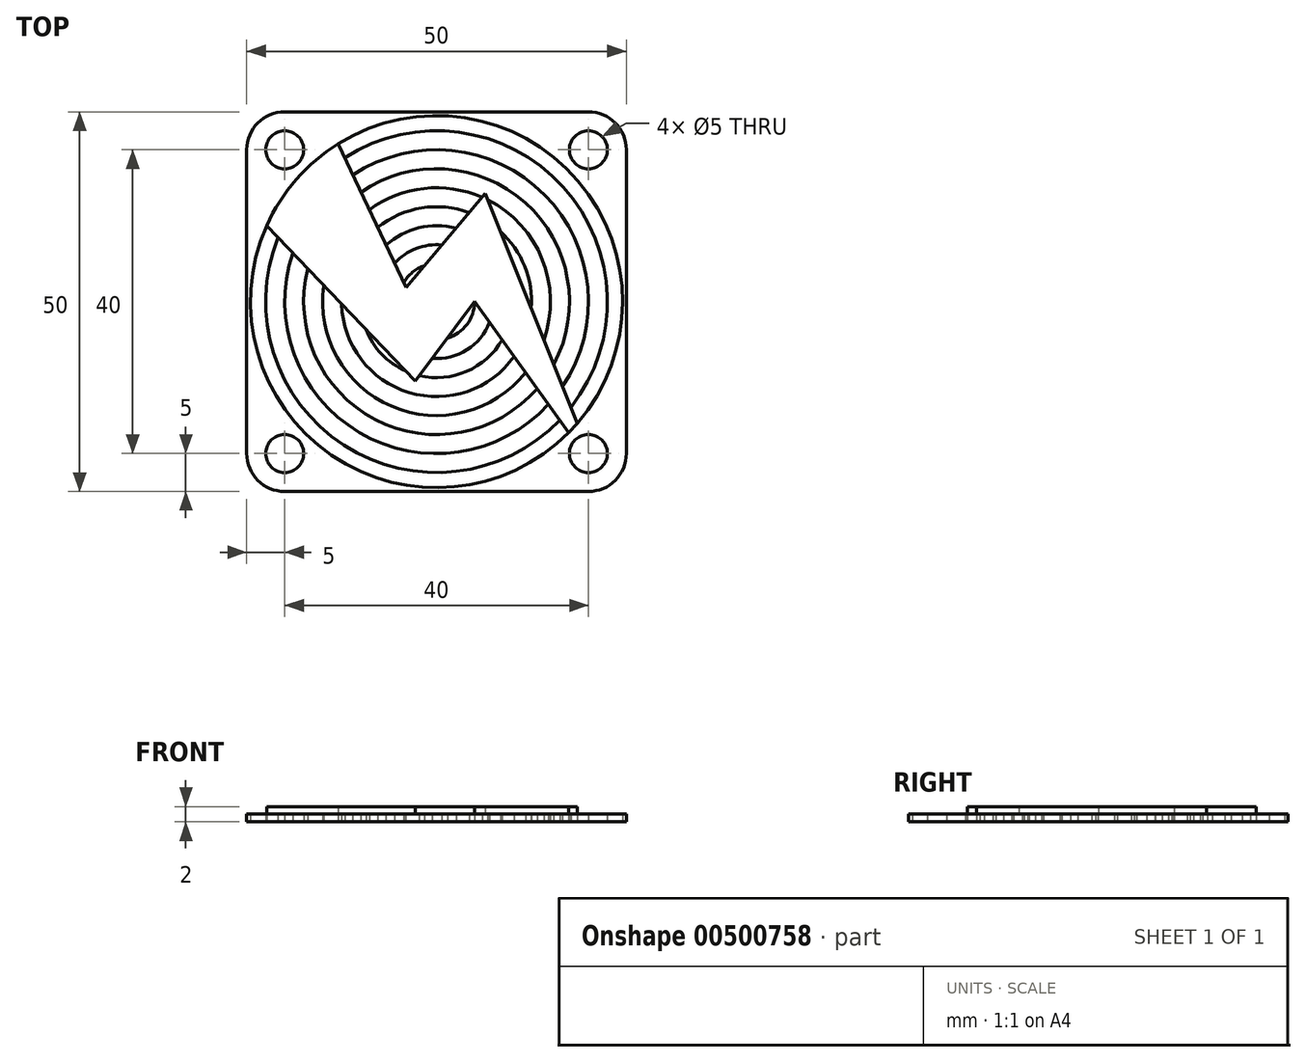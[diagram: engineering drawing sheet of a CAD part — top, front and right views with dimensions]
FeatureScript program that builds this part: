
annotation { "Feature Type Name" : "Feature", "Feature Type Description" : "" }
export const myFeature = defineFeature(function(context is Context, id is Id, definition is map)
    precondition{}
    {
        {
            var Q0;
            Q0=qCreatedBy(makeId("Top.planeOp"),FACE);
            var sketch = newSketch(context, id + "F0", { "sketchPlane" : qUnion([Q0])});
            skLineSegment(sketch, "E0.bottom", {"start": v(-25, 25) * mm, "end": v(25, 25) * mm});
            skLineSegment(sketch, "E0.top", {"start": v(-25, -25) * mm, "end": v(25, -25) * mm});
            skLineSegment(sketch, "E0.left", {"start": v(-25, 25) * mm, "end": v(-25, -25) * mm});
            skLineSegment(sketch, "E0.right", {"start": v(25, 25) * mm, "end": v(25, -25) * mm});
            skCircle(sketch, "E1", {"center": v(20, 20) * mm, "radius": 2.5 * mm});
            skCircle(sketch, "E2", {"center": v(20, -20) * mm, "radius": 2.5 * mm});
            skCircle(sketch, "E3", {"center": v(-20, -20) * mm, "radius": 2.5 * mm});
            skCircle(sketch, "E4", {"center": v(-20, 20) * mm, "radius": 2.5 * mm});
            skCircle(sketch, "E5", {"center": v(0, 0) * mm, "radius": 24.5 * mm});
            skLineSegment(sketch, "E6", {"start": v(-12.96, 20.8) * mm, "end": v(-4.03, 1.85) * mm});
            skLineSegment(sketch, "E7", {"start": v(-4.03, 1.85) * mm, "end": v(6.41, 14.23) * mm});
            skLineSegment(sketch, "E8", {"start": v(6.41, 14.23) * mm, "end": v(21.03, -22.28) * mm});
            skLineSegment(sketch, "E9", {"start": v(21.03, -22.28) * mm, "end": v(5.04, 0) * mm});
            skLineSegment(sketch, "E10", {"start": v(5.04, 0) * mm, "end": v(-2.81, -10.46) * mm});
            skLineSegment(sketch, "E11", {"start": v(-2.81, -10.46) * mm, "end": v(-22.38, 9.98) * mm});
            skCircle(sketch, "E12", {"center": v(0, 0) * mm, "radius": 7.5 * mm});
            skCircle(sketch, "E13", {"center": v(0, 0) * mm, "radius": 10 * mm});
            skCircle(sketch, "E14", {"center": v(0, 0) * mm, "radius": 12.5 * mm});
            skCircle(sketch, "E15", {"center": v(0, 0) * mm, "radius": 15 * mm});
            skCircle(sketch, "E16", {"center": v(0, 0) * mm, "radius": 17.5 * mm});
            skCircle(sketch, "E17", {"center": v(0, 0) * mm, "radius": 20 * mm});
            skCircle(sketch, "E18", {"center": v(0, 0) * mm, "radius": 22.5 * mm});
            skCircle(sketch, "E19", {"center": v(0, 0) * mm, "radius": 5 * mm});
            skCircle(sketch, "E20", {"center": v(-20, 20) * mm, "radius": 3.5 * mm});
            skCircle(sketch, "E21", {"center": v(20, 20) * mm, "radius": 3.5 * mm});
            skCircle(sketch, "E22", {"center": v(20, -20) * mm, "radius": 3.5 * mm});
            skCircle(sketch, "E23", {"center": v(-20, -20) * mm, "radius": 3.5 * mm});
            skSolve(sketch);
        }
        {
            var Q0;
            Q0=makeQuery(id+"F0.imprint","IMPRINT",FACE,{"disambiguationData":[TD([[makeQuery(id+"F0.imprint","IMPRINT",EDGE,{"derivedFrom":sQuery(id+"F0.wireOp",EDGE,"E0.bottom")}),-1.0]])]});
            var Q1;
            {var subQ0=sQuery(id+"F0.wireOp",EDGE,"E6");var subQ1=sQuery(id+"F0.wireOp",EDGE,"E5");var subQ2=makeQuery(id+"F0.imprint","INTERSECT",VERTEX,{"derivedFrom":[subQ1,subQ0]});Q1=makeQuery(id+"F0.imprint","IMPRINT",FACE,{"disambiguationData":[TD([[makeQuery(id+"F0.imprint","IMPRINT",EDGE,{"disambiguationData":[TD([[subQ2,-1.0]])],"derivedFrom":subQ1}),1.0]])]});}
            var Q2;
            {var subQ0=sQuery(id+"F0.wireOp",EDGE,"E18");var subQ1=sQuery(id+"F0.wireOp",EDGE,"E6");var subQ2=makeQuery(id+"F0.imprint","INTERSECT",VERTEX,{"derivedFrom":[subQ1,subQ0]});Q2=makeQuery(id+"F0.imprint","IMPRINT",FACE,{"disambiguationData":[TD([[makeQuery(id+"F0.imprint","IMPRINT",EDGE,{"disambiguationData":[TD([[subQ2,-1.0]])],"derivedFrom":subQ1}),-1.0]])]});}
            var Q3;
            {var subQ0=sQuery(id+"F0.wireOp",EDGE,"E17");var subQ1=sQuery(id+"F0.wireOp",EDGE,"E6");var subQ2=makeQuery(id+"F0.imprint","INTERSECT",VERTEX,{"derivedFrom":[subQ1,subQ0]});Q3=makeQuery(id+"F0.imprint","IMPRINT",FACE,{"disambiguationData":[TD([[makeQuery(id+"F0.imprint","IMPRINT",EDGE,{"disambiguationData":[TD([[subQ2,-1.0]])],"derivedFrom":subQ1}),-1.0]])]});}
            var Q4;
            {var subQ0=sQuery(id+"F0.wireOp",EDGE,"E16");var subQ1=sQuery(id+"F0.wireOp",EDGE,"E6");var subQ2=makeQuery(id+"F0.imprint","INTERSECT",VERTEX,{"derivedFrom":[subQ1,subQ0]});Q4=makeQuery(id+"F0.imprint","IMPRINT",FACE,{"disambiguationData":[TD([[makeQuery(id+"F0.imprint","IMPRINT",EDGE,{"disambiguationData":[TD([[subQ2,-1.0]])],"derivedFrom":subQ1}),-1.0]])]});}
            var Q5;
            {var subQ0=sQuery(id+"F0.wireOp",EDGE,"E15");var subQ1=sQuery(id+"F0.wireOp",EDGE,"E6");var subQ2=makeQuery(id+"F0.imprint","INTERSECT",VERTEX,{"derivedFrom":[subQ1,subQ0]});Q5=makeQuery(id+"F0.imprint","IMPRINT",FACE,{"disambiguationData":[TD([[makeQuery(id+"F0.imprint","IMPRINT",EDGE,{"disambiguationData":[TD([[subQ2,-1.0]])],"derivedFrom":subQ1}),-1.0]])]});}
            var Q6;
            {var subQ0=sQuery(id+"F0.wireOp",EDGE,"E14");var subQ1=sQuery(id+"F0.wireOp",EDGE,"E6");var subQ2=makeQuery(id+"F0.imprint","INTERSECT",VERTEX,{"derivedFrom":[subQ1,subQ0]});Q6=makeQuery(id+"F0.imprint","IMPRINT",FACE,{"disambiguationData":[TD([[makeQuery(id+"F0.imprint","IMPRINT",EDGE,{"disambiguationData":[TD([[subQ2,-1.0]])],"derivedFrom":subQ1}),-1.0]])]});}
            var Q7;
            {var subQ0=sQuery(id+"F0.wireOp",EDGE,"E13");var subQ8=sQuery(id+"F0.wireOp",EDGE,"E6");var subQ10=makeQuery(id+"F0.imprint","INTERSECT",VERTEX,{"derivedFrom":[subQ8,subQ0]});Q7=makeQuery(id+"F0.imprint","IMPRINT",FACE,{"disambiguationData":[TD([[makeQuery(id+"F0.imprint","IMPRINT",EDGE,{"disambiguationData":[TD([[subQ10,-1.0]])],"derivedFrom":subQ8}),-1.0]])]});}
            var Q8;
            {var subQ0=sQuery(id+"F0.wireOp",EDGE,"E12");var subQ1=sQuery(id+"F0.wireOp",EDGE,"E6");var subQ2=makeQuery(id+"F0.imprint","INTERSECT",VERTEX,{"derivedFrom":[subQ1,subQ0]});Q8=makeQuery(id+"F0.imprint","IMPRINT",FACE,{"disambiguationData":[TD([[makeQuery(id+"F0.imprint","IMPRINT",EDGE,{"disambiguationData":[TD([[subQ2,-1.0]])],"derivedFrom":subQ1}),-1.0]])]});}
            var Q9;
            {var subQ1=sQuery(id+"F0.wireOp",EDGE,"E6");var subQ5=sQuery(id+"F0.wireOp",EDGE,"E7");var subQ6=makeQuery(id+"F0.imprint","INTERSECT",VERTEX,{"derivedFrom":[subQ1,subQ5]});Q9=makeQuery(id+"F0.imprint","IMPRINT",FACE,{"disambiguationData":[TD([[makeQuery(id+"F0.imprint","IMPRINT",EDGE,{"disambiguationData":[TD([[subQ6,1.0]])],"derivedFrom":subQ1}),-1.0]])]});}
            var Q10;
            {var subQ1=sQuery(id+"F0.wireOp",EDGE,"E7");var subQ7=sQuery(id+"F0.wireOp",EDGE,"E19");var subQ9=makeQuery(id+"F0.imprint","INTERSECT",VERTEX,{"derivedFrom":[subQ1,subQ7]});Q10=makeQuery(id+"F0.imprint","IMPRINT",FACE,{"disambiguationData":[TD([[makeQuery(id+"F0.imprint","IMPRINT",EDGE,{"disambiguationData":[TD([[subQ9,-1.0]])],"derivedFrom":subQ1}),-1.0]])]});}
            var Q11;
            {var subQ0=sQuery(id+"F0.wireOp",EDGE,"E12");var subQ1=sQuery(id+"F0.wireOp",EDGE,"E7");var subQ2=makeQuery(id+"F0.imprint","INTERSECT",VERTEX,{"derivedFrom":[subQ1,subQ0]});Q11=makeQuery(id+"F0.imprint","IMPRINT",FACE,{"disambiguationData":[TD([[makeQuery(id+"F0.imprint","IMPRINT",EDGE,{"disambiguationData":[TD([[subQ2,-1.0]])],"derivedFrom":subQ1}),-1.0]])]});}
            var Q12;
            {var subQ0=sQuery(id+"F0.wireOp",EDGE,"E13");var subQ1=sQuery(id+"F0.wireOp",EDGE,"E7");var subQ2=makeQuery(id+"F0.imprint","INTERSECT",VERTEX,{"derivedFrom":[subQ1,subQ0]});Q12=makeQuery(id+"F0.imprint","IMPRINT",FACE,{"disambiguationData":[TD([[makeQuery(id+"F0.imprint","IMPRINT",EDGE,{"disambiguationData":[TD([[subQ2,-1.0]])],"derivedFrom":subQ1}),-1.0]])]});}
            var Q13;
            {var subQ0=sQuery(id+"F0.wireOp",EDGE,"E14");var subQ1=sQuery(id+"F0.wireOp",EDGE,"E8");var subQ2=makeQuery(id+"F0.imprint","INTERSECT",VERTEX,{"disambiguationData":[OD(1.0)],"derivedFrom":[subQ1,subQ0]});Q13=makeQuery(id+"F0.imprint","IMPRINT",FACE,{"disambiguationData":[TD([[makeQuery(id+"F0.imprint","IMPRINT",EDGE,{"disambiguationData":[TD([[subQ2,-1.0]])],"derivedFrom":subQ1}),-1.0]])]});}
            var Q14;
            {var subQ0=sQuery(id+"F0.wireOp",EDGE,"E15");var subQ1=sQuery(id+"F0.wireOp",EDGE,"E8");var subQ2=makeQuery(id+"F0.imprint","INTERSECT",VERTEX,{"disambiguationData":[OD(1.0)],"derivedFrom":[subQ1,subQ0]});Q14=makeQuery(id+"F0.imprint","IMPRINT",FACE,{"disambiguationData":[TD([[makeQuery(id+"F0.imprint","IMPRINT",EDGE,{"disambiguationData":[TD([[subQ2,-1.0]])],"derivedFrom":subQ1}),-1.0]])]});}
            var Q15;
            {var subQ0=sQuery(id+"F0.wireOp",EDGE,"E16");var subQ1=sQuery(id+"F0.wireOp",EDGE,"E8");var subQ2=makeQuery(id+"F0.imprint","INTERSECT",VERTEX,{"derivedFrom":[subQ1,subQ0]});Q15=makeQuery(id+"F0.imprint","IMPRINT",FACE,{"disambiguationData":[TD([[makeQuery(id+"F0.imprint","IMPRINT",EDGE,{"disambiguationData":[TD([[subQ2,-1.0]])],"derivedFrom":subQ1}),-1.0]])]});}
            var Q16;
            {var subQ0=sQuery(id+"F0.wireOp",EDGE,"E17");var subQ1=sQuery(id+"F0.wireOp",EDGE,"E8");var subQ2=makeQuery(id+"F0.imprint","INTERSECT",VERTEX,{"derivedFrom":[subQ1,subQ0]});Q16=makeQuery(id+"F0.imprint","IMPRINT",FACE,{"disambiguationData":[TD([[makeQuery(id+"F0.imprint","IMPRINT",EDGE,{"disambiguationData":[TD([[subQ2,-1.0]])],"derivedFrom":subQ1}),-1.0]])]});}
            var Q17;
            {var subQ0=sQuery(id+"F0.wireOp",EDGE,"E9");var subQ1=sQuery(id+"F0.wireOp",EDGE,"E5");var subQ2=makeQuery(id+"F0.imprint","INTERSECT",VERTEX,{"derivedFrom":[subQ1,subQ0]});Q17=makeQuery(id+"F0.imprint","IMPRINT",FACE,{"disambiguationData":[TD([[makeQuery(id+"F0.imprint","IMPRINT",EDGE,{"disambiguationData":[TD([[subQ2,-1.0]])],"derivedFrom":subQ1}),1.0]])]});}
            var Q18;
            {var subQ0=sQuery(id+"F0.wireOp",EDGE,"E9");var subQ1=sQuery(id+"F0.wireOp",EDGE,"E5");var subQ2=makeQuery(id+"F0.imprint","INTERSECT",VERTEX,{"derivedFrom":[subQ1,subQ0]});Q18=makeQuery(id+"F0.imprint","IMPRINT",FACE,{"disambiguationData":[TD([[makeQuery(id+"F0.imprint","IMPRINT",EDGE,{"disambiguationData":[TD([[subQ2,-1.0]])],"derivedFrom":subQ1}),-1.0]])]});}
            var Q19;
            {var subQ0=sQuery(id+"F0.wireOp",EDGE,"E8");var subQ1=sQuery(id+"F0.wireOp",EDGE,"E2");var subQ2=makeQuery(id+"F0.imprint","INTERSECT",VERTEX,{"derivedFrom":[subQ1,subQ0]});Q19=makeQuery(id+"F0.imprint","IMPRINT",FACE,{"disambiguationData":[TD([[makeQuery(id+"F0.imprint","IMPRINT",EDGE,{"disambiguationData":[TD([[subQ2,1.0]])],"derivedFrom":subQ0}),1.0]])]});}
            var Q20;
            {var subQ0=sQuery(id+"F0.wireOp",EDGE,"E9");var subQ1=sQuery(id+"F0.wireOp",EDGE,"E2");var subQ2=makeQuery(id+"F0.imprint","INTERSECT",VERTEX,{"derivedFrom":[subQ1,subQ0]});Q20=makeQuery(id+"F0.imprint","IMPRINT",FACE,{"disambiguationData":[TD([[makeQuery(id+"F0.imprint","IMPRINT",EDGE,{"disambiguationData":[TD([[subQ2,1.0]])],"derivedFrom":subQ1}),-1.0]])]});}
            var Q21;
            Q21=makeQuery(id+"F0.imprint","IMPRINT",FACE,{"disambiguationData":[TD([[makeQuery(id+"F0.imprint","IMPRINT",EDGE,{"derivedFrom":sQuery(id+"F0.wireOp",EDGE,"E3")}),-1.0]])]});
            var Q22;
            Q22=makeQuery(id+"F0.imprint","IMPRINT",FACE,{"disambiguationData":[TD([[makeQuery(id+"F0.imprint","IMPRINT",EDGE,{"derivedFrom":sQuery(id+"F0.wireOp",EDGE,"E1")}),-1.0]])]});
            var Q23;
            Q23=makeQuery(id+"F0.imprint","IMPRINT",FACE,{"disambiguationData":[TD([[makeQuery(id+"F0.imprint","IMPRINT",EDGE,{"derivedFrom":sQuery(id+"F0.wireOp",EDGE,"E4")}),-1.0]])]});
            var Q24;
            {var subQ0=sQuery(id+"F0.wireOp",EDGE,"E14");var subQ1=sQuery(id+"F0.wireOp",EDGE,"E7");var subQ2=makeQuery(id+"F0.imprint","INTERSECT",VERTEX,{"derivedFrom":[subQ1,subQ0]});Q24=makeQuery(id+"F0.imprint","IMPRINT",FACE,{"disambiguationData":[TD([[makeQuery(id+"F0.imprint","IMPRINT",EDGE,{"disambiguationData":[TD([[subQ2,-1.0]])],"derivedFrom":subQ1}),-1.0]])]});}
            var Q25;
            {var subQ0=sQuery(id+"F0.wireOp",EDGE,"E8");var subQ1=sQuery(id+"F0.wireOp",EDGE,"E7");var subQ2=makeQuery(id+"F0.imprint","INTERSECT",VERTEX,{"derivedFrom":[subQ1,subQ0]});Q25=makeQuery(id+"F0.imprint","IMPRINT",FACE,{"disambiguationData":[TD([[makeQuery(id+"F0.imprint","IMPRINT",EDGE,{"disambiguationData":[TD([[subQ2,1.0]])],"derivedFrom":subQ1}),-1.0]])]});}
            var Q26;
            {var subQ0=sQuery(id+"F0.wireOp",EDGE,"E11");var subQ1=sQuery(id+"F0.wireOp",EDGE,"E10");var subQ2=makeQuery(id+"F0.imprint","INTERSECT",VERTEX,{"derivedFrom":[subQ1,subQ0]});Q26=makeQuery(id+"F0.imprint","IMPRINT",FACE,{"disambiguationData":[TD([[makeQuery(id+"F0.imprint","IMPRINT",EDGE,{"disambiguationData":[TD([[subQ2,1.0]])],"derivedFrom":subQ1}),-1.0]])]});}
            var Q27;
            {var subQ0=sQuery(id+"F0.wireOp",EDGE,"E18");var subQ1=sQuery(id+"F0.wireOp",EDGE,"E9");var subQ2=makeQuery(id+"F0.imprint","INTERSECT",VERTEX,{"derivedFrom":[subQ1,subQ0]});Q27=makeQuery(id+"F0.imprint","IMPRINT",FACE,{"disambiguationData":[TD([[makeQuery(id+"F0.imprint","IMPRINT",EDGE,{"disambiguationData":[TD([[subQ2,-1.0]])],"derivedFrom":subQ1}),1.0]])]});}
            var Q28;
            {var subQ0=sQuery(id+"F0.wireOp",EDGE,"E16");var subQ1=sQuery(id+"F0.wireOp",EDGE,"E9");var subQ2=makeQuery(id+"F0.imprint","INTERSECT",VERTEX,{"derivedFrom":[subQ1,subQ0]});Q28=makeQuery(id+"F0.imprint","IMPRINT",FACE,{"disambiguationData":[TD([[makeQuery(id+"F0.imprint","IMPRINT",EDGE,{"disambiguationData":[TD([[subQ2,-1.0]])],"derivedFrom":subQ1}),1.0]])]});}
            var Q29;
            {var subQ6=sQuery(id+"F0.wireOp",EDGE,"E14");var subQ7=sQuery(id+"F0.wireOp",EDGE,"E9");var subQ8=makeQuery(id+"F0.imprint","INTERSECT",VERTEX,{"derivedFrom":[subQ7,subQ6]});Q29=makeQuery(id+"F0.imprint","IMPRINT",FACE,{"disambiguationData":[TD([[makeQuery(id+"F0.imprint","IMPRINT",EDGE,{"disambiguationData":[TD([[subQ8,-1.0]])],"derivedFrom":subQ7}),1.0]])]});}
            var Q30;
            {var subQ1=sQuery(id+"F0.wireOp",EDGE,"E10");var subQ5=sQuery(id+"F0.wireOp",EDGE,"E9");var subQ7=makeQuery(id+"F0.imprint","INTERSECT",VERTEX,{"derivedFrom":[subQ5,subQ1]});Q30=makeQuery(id+"F0.imprint","IMPRINT",FACE,{"disambiguationData":[TD([[makeQuery(id+"F0.imprint","IMPRINT",EDGE,{"disambiguationData":[TD([[subQ7,1.0]])],"derivedFrom":subQ5}),1.0]])]});}
            var Q31;
            {var subQ0=sQuery(id+"F0.wireOp",EDGE,"E18");var subQ1=sQuery(id+"F0.wireOp",EDGE,"E6");var subQ2=makeQuery(id+"F0.imprint","INTERSECT",VERTEX,{"derivedFrom":[subQ1,subQ0]});Q31=makeQuery(id+"F0.imprint","IMPRINT",FACE,{"disambiguationData":[TD([[makeQuery(id+"F0.imprint","IMPRINT",EDGE,{"disambiguationData":[TD([[subQ2,-1.0]])],"derivedFrom":subQ1}),1.0]])]});}
            var Q32;
            {var subQ6=sQuery(id+"F0.wireOp",EDGE,"E16");var subQ9=sQuery(id+"F0.wireOp",EDGE,"E6");var subQ10=makeQuery(id+"F0.imprint","INTERSECT",VERTEX,{"derivedFrom":[subQ9,subQ6]});Q32=makeQuery(id+"F0.imprint","IMPRINT",FACE,{"disambiguationData":[TD([[makeQuery(id+"F0.imprint","IMPRINT",EDGE,{"disambiguationData":[TD([[subQ10,-1.0]])],"derivedFrom":subQ9}),1.0]])]});}
            var Q33;
            {var subQ0=sQuery(id+"F0.wireOp",EDGE,"E14");var subQ1=sQuery(id+"F0.wireOp",EDGE,"E8");var subQ2=makeQuery(id+"F0.imprint","INTERSECT",VERTEX,{"disambiguationData":[OD(0.0)],"derivedFrom":[subQ1,subQ0]});Q33=makeQuery(id+"F0.imprint","IMPRINT",FACE,{"disambiguationData":[TD([[makeQuery(id+"F0.imprint","IMPRINT",EDGE,{"disambiguationData":[TD([[subQ2,-1.0]])],"derivedFrom":subQ1}),1.0]])]});}
            var Q34;
            {var subQ0=sQuery(id+"F0.wireOp",EDGE,"E14");var subQ1=sQuery(id+"F0.wireOp",EDGE,"E6");var subQ2=makeQuery(id+"F0.imprint","INTERSECT",VERTEX,{"derivedFrom":[subQ1,subQ0]});Q34=makeQuery(id+"F0.imprint","IMPRINT",FACE,{"disambiguationData":[TD([[makeQuery(id+"F0.imprint","IMPRINT",EDGE,{"disambiguationData":[TD([[subQ2,-1.0]])],"derivedFrom":subQ1}),1.0]])]});}
            var Q35;
            {var subQ0=sQuery(id+"F0.wireOp",EDGE,"E12");var subQ1=sQuery(id+"F0.wireOp",EDGE,"E6");var subQ2=makeQuery(id+"F0.imprint","INTERSECT",VERTEX,{"derivedFrom":[subQ1,subQ0]});Q35=makeQuery(id+"F0.imprint","IMPRINT",FACE,{"disambiguationData":[TD([[makeQuery(id+"F0.imprint","IMPRINT",EDGE,{"disambiguationData":[TD([[subQ2,-1.0]])],"derivedFrom":subQ1}),1.0]])]});}
            extrude(context, id + "F1", {"entities" : qUnion([Q0, Q1, Q2, Q3, Q4, Q5, Q6, Q7, Q8, Q9, Q10, Q11, Q12, Q13, Q14, Q15, Q16, Q17, Q18, Q19, Q20, Q21, Q22, Q23, Q24, Q25, Q26, Q27, Q28, Q29, Q30, Q31, Q32, Q33, Q34, Q35]), "depth" : 1 * mm});
        }
        {
            var Q0;
            {var subQ0=sQuery(id+"F0.wireOp",EDGE,"E9");var subQ1=sQuery(id+"F0.wireOp",EDGE,"E5");var subQ2=makeQuery(id+"F0.imprint","INTERSECT",VERTEX,{"derivedFrom":[subQ1,subQ0]});Q0=makeQuery(id+"F0.imprint","IMPRINT",FACE,{"disambiguationData":[TD([[makeQuery(id+"F0.imprint","IMPRINT",EDGE,{"disambiguationData":[TD([[subQ2,-1.0]])],"derivedFrom":subQ1}),1.0]])]});}
            var Q1;
            {var subQ0=sQuery(id+"F0.wireOp",EDGE,"E17");var subQ1=sQuery(id+"F0.wireOp",EDGE,"E8");var subQ2=makeQuery(id+"F0.imprint","INTERSECT",VERTEX,{"derivedFrom":[subQ1,subQ0]});Q1=makeQuery(id+"F0.imprint","IMPRINT",FACE,{"disambiguationData":[TD([[makeQuery(id+"F0.imprint","IMPRINT",EDGE,{"disambiguationData":[TD([[subQ2,-1.0]])],"derivedFrom":subQ1}),-1.0]])]});}
            var Q2;
            {var subQ0=sQuery(id+"F0.wireOp",EDGE,"E16");var subQ1=sQuery(id+"F0.wireOp",EDGE,"E8");var subQ2=makeQuery(id+"F0.imprint","INTERSECT",VERTEX,{"derivedFrom":[subQ1,subQ0]});Q2=makeQuery(id+"F0.imprint","IMPRINT",FACE,{"disambiguationData":[TD([[makeQuery(id+"F0.imprint","IMPRINT",EDGE,{"disambiguationData":[TD([[subQ2,-1.0]])],"derivedFrom":subQ1}),-1.0]])]});}
            var Q3;
            {var subQ0=sQuery(id+"F0.wireOp",EDGE,"E15");var subQ1=sQuery(id+"F0.wireOp",EDGE,"E8");var subQ2=makeQuery(id+"F0.imprint","INTERSECT",VERTEX,{"disambiguationData":[OD(1.0)],"derivedFrom":[subQ1,subQ0]});Q3=makeQuery(id+"F0.imprint","IMPRINT",FACE,{"disambiguationData":[TD([[makeQuery(id+"F0.imprint","IMPRINT",EDGE,{"disambiguationData":[TD([[subQ2,-1.0]])],"derivedFrom":subQ1}),-1.0]])]});}
            var Q4;
            {var subQ0=sQuery(id+"F0.wireOp",EDGE,"E14");var subQ1=sQuery(id+"F0.wireOp",EDGE,"E8");var subQ2=makeQuery(id+"F0.imprint","INTERSECT",VERTEX,{"disambiguationData":[OD(1.0)],"derivedFrom":[subQ1,subQ0]});Q4=makeQuery(id+"F0.imprint","IMPRINT",FACE,{"disambiguationData":[TD([[makeQuery(id+"F0.imprint","IMPRINT",EDGE,{"disambiguationData":[TD([[subQ2,-1.0]])],"derivedFrom":subQ1}),-1.0]])]});}
            var Q5;
            {var subQ0=sQuery(id+"F0.wireOp",EDGE,"E13");var subQ1=sQuery(id+"F0.wireOp",EDGE,"E7");var subQ2=makeQuery(id+"F0.imprint","INTERSECT",VERTEX,{"derivedFrom":[subQ1,subQ0]});Q5=makeQuery(id+"F0.imprint","IMPRINT",FACE,{"disambiguationData":[TD([[makeQuery(id+"F0.imprint","IMPRINT",EDGE,{"disambiguationData":[TD([[subQ2,-1.0]])],"derivedFrom":subQ1}),-1.0]])]});}
            var Q6;
            {var subQ0=sQuery(id+"F0.wireOp",EDGE,"E12");var subQ1=sQuery(id+"F0.wireOp",EDGE,"E7");var subQ2=makeQuery(id+"F0.imprint","INTERSECT",VERTEX,{"derivedFrom":[subQ1,subQ0]});Q6=makeQuery(id+"F0.imprint","IMPRINT",FACE,{"disambiguationData":[TD([[makeQuery(id+"F0.imprint","IMPRINT",EDGE,{"disambiguationData":[TD([[subQ2,-1.0]])],"derivedFrom":subQ1}),-1.0]])]});}
            var Q7;
            {var subQ1=sQuery(id+"F0.wireOp",EDGE,"E7");var subQ7=sQuery(id+"F0.wireOp",EDGE,"E19");var subQ9=makeQuery(id+"F0.imprint","INTERSECT",VERTEX,{"derivedFrom":[subQ1,subQ7]});Q7=makeQuery(id+"F0.imprint","IMPRINT",FACE,{"disambiguationData":[TD([[makeQuery(id+"F0.imprint","IMPRINT",EDGE,{"disambiguationData":[TD([[subQ9,-1.0]])],"derivedFrom":subQ1}),-1.0]])]});}
            var Q8;
            {var subQ1=sQuery(id+"F0.wireOp",EDGE,"E6");var subQ5=sQuery(id+"F0.wireOp",EDGE,"E7");var subQ6=makeQuery(id+"F0.imprint","INTERSECT",VERTEX,{"derivedFrom":[subQ1,subQ5]});Q8=makeQuery(id+"F0.imprint","IMPRINT",FACE,{"disambiguationData":[TD([[makeQuery(id+"F0.imprint","IMPRINT",EDGE,{"disambiguationData":[TD([[subQ6,1.0]])],"derivedFrom":subQ1}),-1.0]])]});}
            var Q9;
            {var subQ0=sQuery(id+"F0.wireOp",EDGE,"E12");var subQ1=sQuery(id+"F0.wireOp",EDGE,"E6");var subQ2=makeQuery(id+"F0.imprint","INTERSECT",VERTEX,{"derivedFrom":[subQ1,subQ0]});Q9=makeQuery(id+"F0.imprint","IMPRINT",FACE,{"disambiguationData":[TD([[makeQuery(id+"F0.imprint","IMPRINT",EDGE,{"disambiguationData":[TD([[subQ2,-1.0]])],"derivedFrom":subQ1}),-1.0]])]});}
            var Q10;
            {var subQ0=sQuery(id+"F0.wireOp",EDGE,"E13");var subQ8=sQuery(id+"F0.wireOp",EDGE,"E6");var subQ10=makeQuery(id+"F0.imprint","INTERSECT",VERTEX,{"derivedFrom":[subQ8,subQ0]});Q10=makeQuery(id+"F0.imprint","IMPRINT",FACE,{"disambiguationData":[TD([[makeQuery(id+"F0.imprint","IMPRINT",EDGE,{"disambiguationData":[TD([[subQ10,-1.0]])],"derivedFrom":subQ8}),-1.0]])]});}
            var Q11;
            {var subQ0=sQuery(id+"F0.wireOp",EDGE,"E14");var subQ1=sQuery(id+"F0.wireOp",EDGE,"E6");var subQ2=makeQuery(id+"F0.imprint","INTERSECT",VERTEX,{"derivedFrom":[subQ1,subQ0]});Q11=makeQuery(id+"F0.imprint","IMPRINT",FACE,{"disambiguationData":[TD([[makeQuery(id+"F0.imprint","IMPRINT",EDGE,{"disambiguationData":[TD([[subQ2,-1.0]])],"derivedFrom":subQ1}),-1.0]])]});}
            var Q12;
            {var subQ0=sQuery(id+"F0.wireOp",EDGE,"E15");var subQ1=sQuery(id+"F0.wireOp",EDGE,"E6");var subQ2=makeQuery(id+"F0.imprint","INTERSECT",VERTEX,{"derivedFrom":[subQ1,subQ0]});Q12=makeQuery(id+"F0.imprint","IMPRINT",FACE,{"disambiguationData":[TD([[makeQuery(id+"F0.imprint","IMPRINT",EDGE,{"disambiguationData":[TD([[subQ2,-1.0]])],"derivedFrom":subQ1}),-1.0]])]});}
            var Q13;
            {var subQ0=sQuery(id+"F0.wireOp",EDGE,"E16");var subQ1=sQuery(id+"F0.wireOp",EDGE,"E6");var subQ2=makeQuery(id+"F0.imprint","INTERSECT",VERTEX,{"derivedFrom":[subQ1,subQ0]});Q13=makeQuery(id+"F0.imprint","IMPRINT",FACE,{"disambiguationData":[TD([[makeQuery(id+"F0.imprint","IMPRINT",EDGE,{"disambiguationData":[TD([[subQ2,-1.0]])],"derivedFrom":subQ1}),-1.0]])]});}
            var Q14;
            {var subQ0=sQuery(id+"F0.wireOp",EDGE,"E17");var subQ1=sQuery(id+"F0.wireOp",EDGE,"E6");var subQ2=makeQuery(id+"F0.imprint","INTERSECT",VERTEX,{"derivedFrom":[subQ1,subQ0]});Q14=makeQuery(id+"F0.imprint","IMPRINT",FACE,{"disambiguationData":[TD([[makeQuery(id+"F0.imprint","IMPRINT",EDGE,{"disambiguationData":[TD([[subQ2,-1.0]])],"derivedFrom":subQ1}),-1.0]])]});}
            var Q15;
            {var subQ0=sQuery(id+"F0.wireOp",EDGE,"E18");var subQ1=sQuery(id+"F0.wireOp",EDGE,"E6");var subQ2=makeQuery(id+"F0.imprint","INTERSECT",VERTEX,{"derivedFrom":[subQ1,subQ0]});Q15=makeQuery(id+"F0.imprint","IMPRINT",FACE,{"disambiguationData":[TD([[makeQuery(id+"F0.imprint","IMPRINT",EDGE,{"disambiguationData":[TD([[subQ2,-1.0]])],"derivedFrom":subQ1}),-1.0]])]});}
            var Q16;
            {var subQ0=sQuery(id+"F0.wireOp",EDGE,"E6");var subQ1=sQuery(id+"F0.wireOp",EDGE,"E5");var subQ2=makeQuery(id+"F0.imprint","INTERSECT",VERTEX,{"derivedFrom":[subQ1,subQ0]});Q16=makeQuery(id+"F0.imprint","IMPRINT",FACE,{"disambiguationData":[TD([[makeQuery(id+"F0.imprint","IMPRINT",EDGE,{"disambiguationData":[TD([[subQ2,-1.0]])],"derivedFrom":subQ1}),1.0]])]});}
            var Q17;
            {var subQ0=sQuery(id+"F0.wireOp",EDGE,"E11");var subQ1=sQuery(id+"F0.wireOp",EDGE,"E10");var subQ2=makeQuery(id+"F0.imprint","INTERSECT",VERTEX,{"derivedFrom":[subQ1,subQ0]});Q17=makeQuery(id+"F0.imprint","IMPRINT",FACE,{"disambiguationData":[TD([[makeQuery(id+"F0.imprint","IMPRINT",EDGE,{"disambiguationData":[TD([[subQ2,1.0]])],"derivedFrom":subQ1}),-1.0]])]});}
            var Q18;
            {var subQ0=sQuery(id+"F0.wireOp",EDGE,"E14");var subQ1=sQuery(id+"F0.wireOp",EDGE,"E7");var subQ2=makeQuery(id+"F0.imprint","INTERSECT",VERTEX,{"derivedFrom":[subQ1,subQ0]});Q18=makeQuery(id+"F0.imprint","IMPRINT",FACE,{"disambiguationData":[TD([[makeQuery(id+"F0.imprint","IMPRINT",EDGE,{"disambiguationData":[TD([[subQ2,-1.0]])],"derivedFrom":subQ1}),-1.0]])]});}
            var Q19;
            {var subQ0=sQuery(id+"F0.wireOp",EDGE,"E8");var subQ1=sQuery(id+"F0.wireOp",EDGE,"E7");var subQ2=makeQuery(id+"F0.imprint","INTERSECT",VERTEX,{"derivedFrom":[subQ1,subQ0]});Q19=makeQuery(id+"F0.imprint","IMPRINT",FACE,{"disambiguationData":[TD([[makeQuery(id+"F0.imprint","IMPRINT",EDGE,{"disambiguationData":[TD([[subQ2,1.0]])],"derivedFrom":subQ1}),-1.0]])]});}
            extrude(context, id + "F2", {"entities" : qUnion([Q0, Q1, Q2, Q3, Q4, Q5, Q6, Q7, Q8, Q9, Q10, Q11, Q12, Q13, Q14, Q15, Q16, Q17, Q18, Q19]), "operationType" : NewBodyOperationType.ADD, "depth" : 2 * mm});
        }
        {
            var Q0;
            Q0=makeQuery(id+"F1.opExtrude","SWEPT_EDGE",EDGE,{"disambiguationData":[OSD([sQuery(id+"F0.wireOp",EDGE,"E0.bottom"),sQuery(id+"F0.wireOp",EDGE,"E0.right")])]});
            var Q1;
            Q1=makeQuery(id+"F1.opExtrude","SWEPT_EDGE",EDGE,{"disambiguationData":[OSD([sQuery(id+"F0.wireOp",EDGE,"E0.top"),sQuery(id+"F0.wireOp",EDGE,"E0.right")])]});
            var Q2;
            Q2=makeQuery(id+"F1.opExtrude","SWEPT_EDGE",EDGE,{"disambiguationData":[OSD([sQuery(id+"F0.wireOp",EDGE,"E0.top"),sQuery(id+"F0.wireOp",EDGE,"E0.left")])]});
            var Q3;
            Q3=makeQuery(id+"F1.opExtrude","SWEPT_EDGE",EDGE,{"disambiguationData":[OSD([sQuery(id+"F0.wireOp",EDGE,"E0.bottom"),sQuery(id+"F0.wireOp",EDGE,"E0.left")])]});
            fillet(context, id + "F3", {"entities" : qUnion([Q0, Q1, Q2, Q3]), "radius" : 5 * mm, "tangentPropagation" : true, "allowEdgeOverflow" : false});
        }
    });
